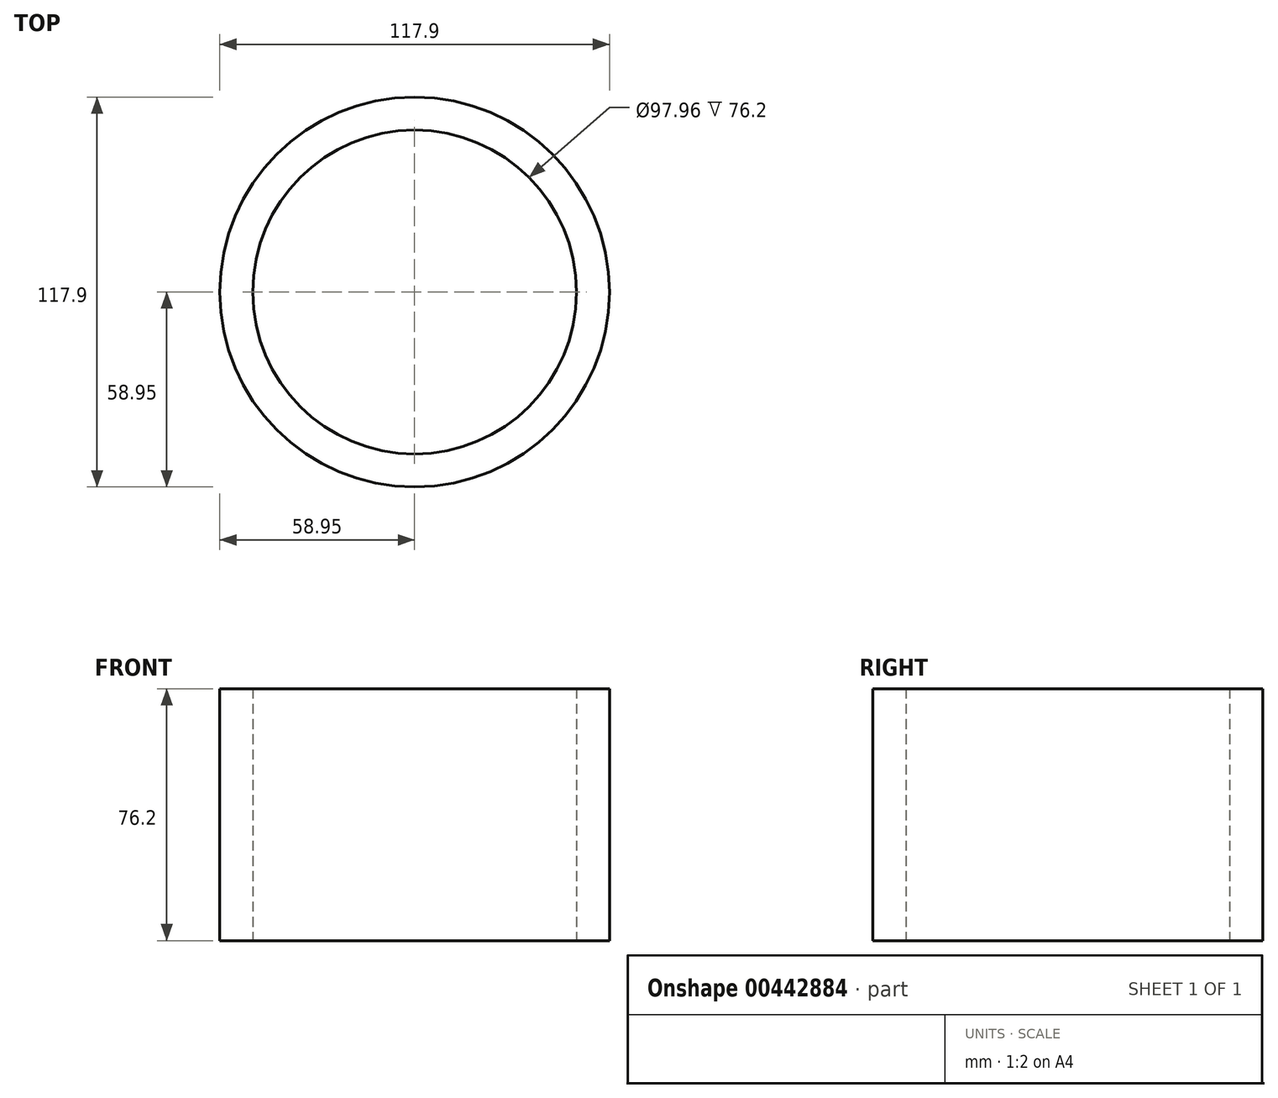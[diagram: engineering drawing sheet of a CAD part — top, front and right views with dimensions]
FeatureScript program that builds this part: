
annotation { "Feature Type Name" : "Feature", "Feature Type Description" : "" }
export const myFeature = defineFeature(function(context is Context, id is Id, definition is map)
    precondition{}
    {
        {
            var Q0;
            Q0=qCreatedBy(makeId("Top.planeOp"),FACE);
            var sketch = newSketch(context, id + "F0", { "sketchPlane" : qUnion([Q0])});
            skCircle(sketch, "E0", {"center": v(0, 0) * mm, "radius": 58.95 * mm});
            skCircle(sketch, "E1", {"center": v(0, 0) * mm, "radius": 48.98 * mm});
            skSolve(sketch);
        }
        {
            var Q0;
            Q0 = qSketchRegion(id + "F0", true);
            extrude(context, id + "F1", {"entities" : qUnion([Q0]), "depth" : 25.4 * mm});
        }
        {
            var Q0;
            Q0=makeQuery(id+"F1.opExtrude","CAP_FACE",FACE,{"disambiguationData":[OSD([sQuery(id+"F0.wireOp",EDGE,"E0"),sQuery(id+"F0.wireOp",EDGE,"E1")])],"isStart":false});
            var Q1;
            Q1=makeQuery(id+"F1.opExtrude","CAP_FACE",FACE,{"disambiguationData":[OSD([sQuery(id+"F0.wireOp",EDGE,"E0"),sQuery(id+"F0.wireOp",EDGE,"E1")])],"isStart":true});
            extrude(context, id + "F2", {"entities" : qUnion([Q0, Q1]), "operationType" : NewBodyOperationType.ADD, "depth" : 25.4 * mm});
        }
        {
            var Q0;
            {var subQ0=sQuery(id+"F0.wireOp",EDGE,"E1");var subQ1=sQuery(id+"F0.wireOp",EDGE,"E0");Q0=makeQuery(id+"F2.opExtrude","CAP_FACE",FACE,{"disambiguationData":[OSD([subQ1,subQ0]),TDD([makeQuery(id+"F1.opExtrude","CAP_FACE",FACE,{"disambiguationData":[OSD([subQ1,subQ0])],"isStart":false})])],"isStart":false});}
            extrude(context, id + "F3", {"entities" : qUnion([Q0]), "operationType" : NewBodyOperationType.ADD, "depth" : 25.4 * mm});
        }
    });
